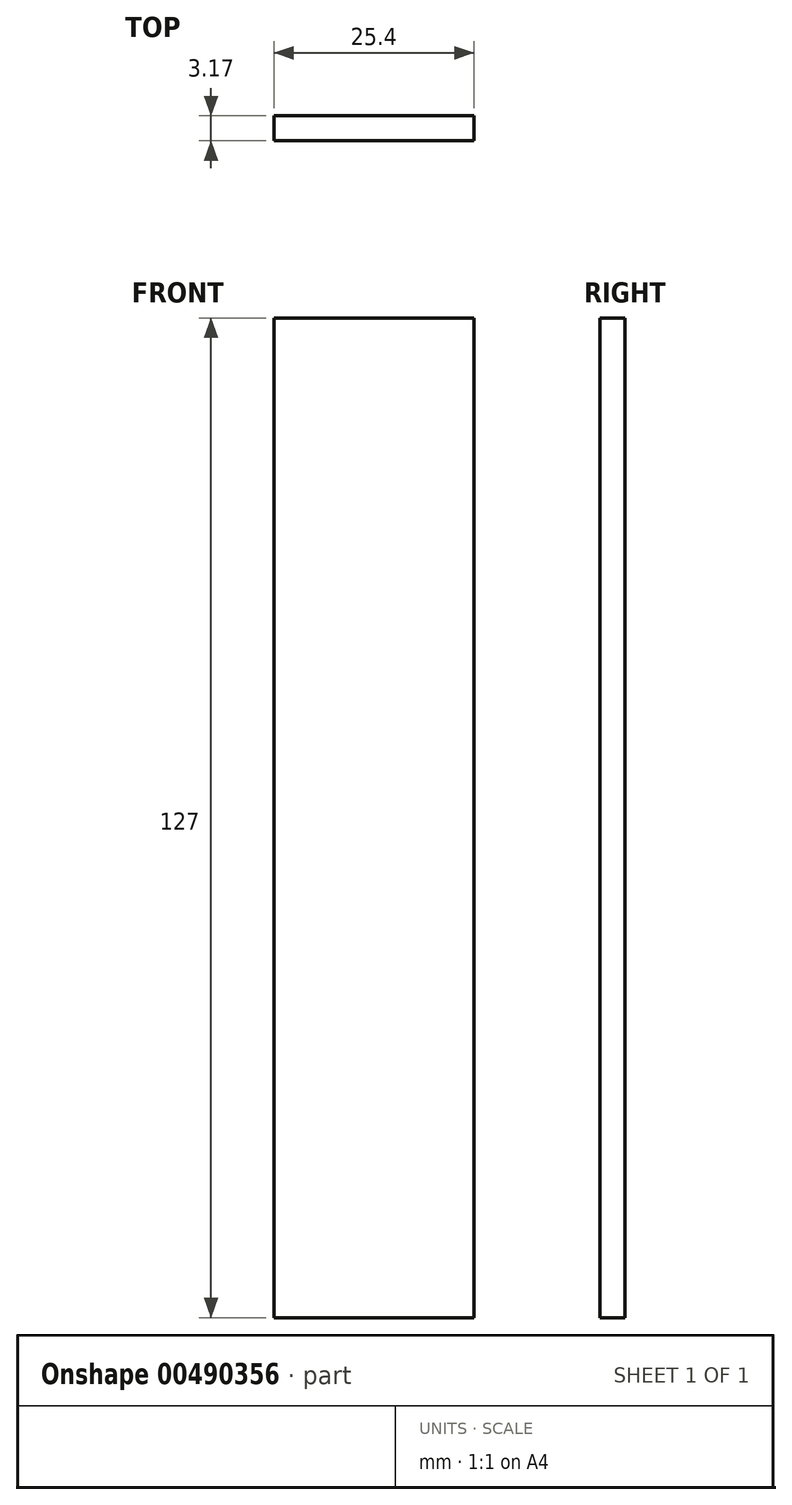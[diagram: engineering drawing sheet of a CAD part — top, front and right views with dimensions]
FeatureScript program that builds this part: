
annotation { "Feature Type Name" : "Feature", "Feature Type Description" : "" }
export const myFeature = defineFeature(function(context is Context, id is Id, definition is map)
    precondition{}
    {
        {
            var Q0;
            Q0=qCreatedBy(makeId("Front.planeOp"),FACE);
            var sketch = newSketch(context, id + "F0", { "sketchPlane" : qUnion([Q0])});
            skLineSegment(sketch, "E0.bottom", {"start": v(25.4, -42.03) * mm, "end": v(0, -42.03) * mm});
            skLineSegment(sketch, "E0.top", {"start": v(25.4, 84.97) * mm, "end": v(0, 84.97) * mm});
            skLineSegment(sketch, "E0.left", {"start": v(25.4, -42.03) * mm, "end": v(25.4, 84.97) * mm});
            skLineSegment(sketch, "E0.right", {"start": v(0, -42.03) * mm, "end": v(0, 84.97) * mm});
            skSolve(sketch);
        }
        {
            var Q0;
            Q0=makeQuery(id+"F0.imprint","IMPRINT",FACE,{"disambiguationData":[TD([[makeQuery(id+"F0.imprint","IMPRINT",EDGE,{"derivedFrom":sQuery(id+"F0.wireOp",EDGE,"E0.bottom")}),-1.0]])]});
            extrude(context, id + "F1", {"entities" : qUnion([Q0]), "depth" : 3.17 * mm});
        }
    });
